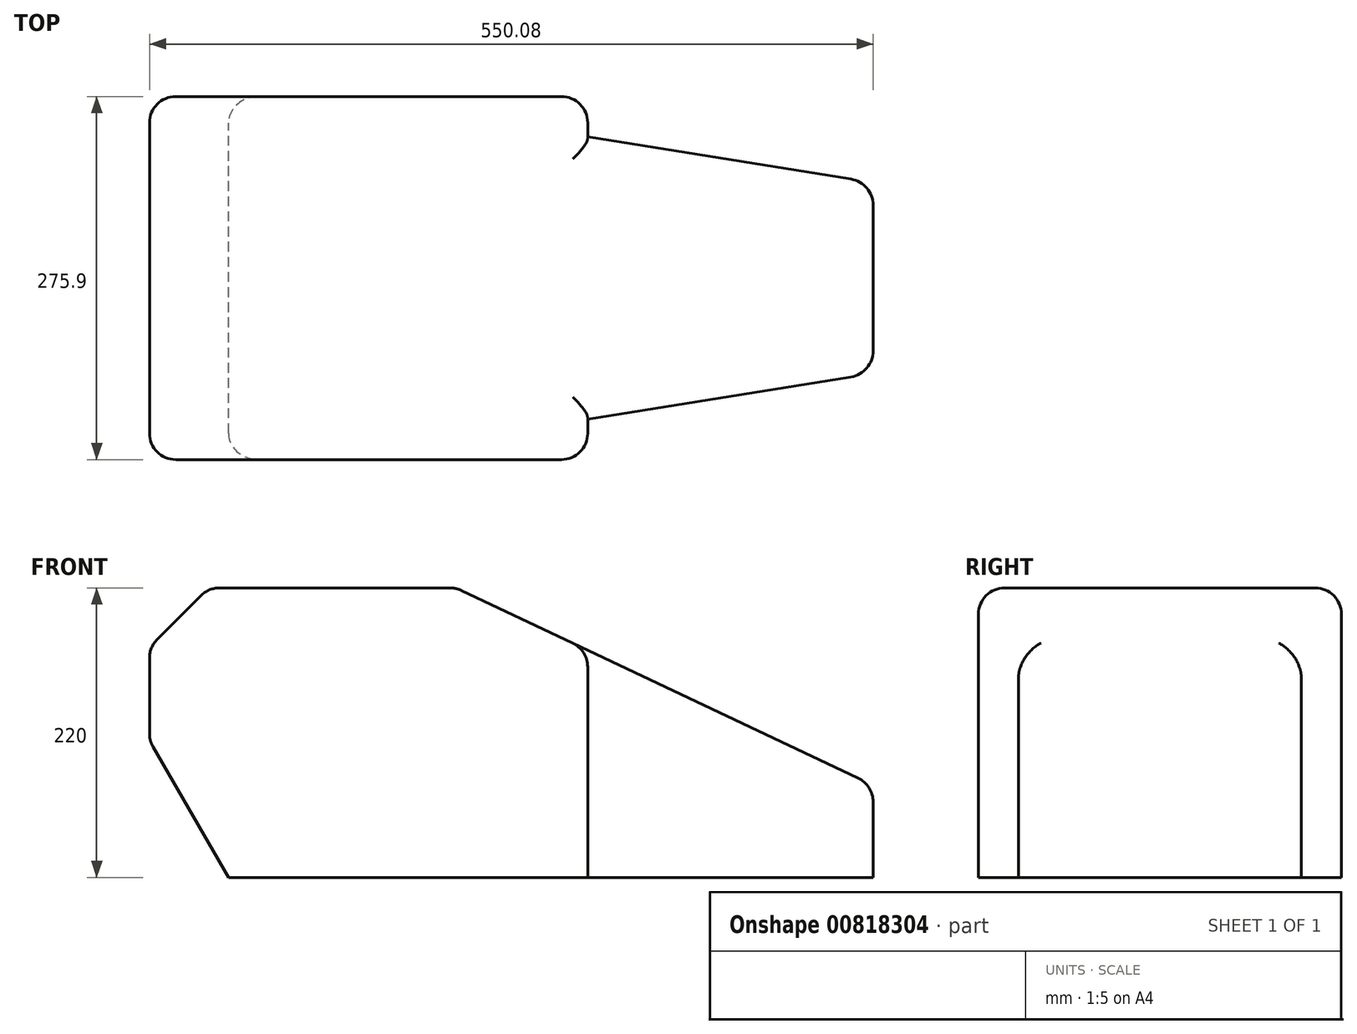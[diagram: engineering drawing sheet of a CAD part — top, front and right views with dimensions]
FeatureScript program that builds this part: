
annotation { "Feature Type Name" : "Feature", "Feature Type Description" : "" }
export const myFeature = defineFeature(function(context is Context, id is Id, definition is map)
    precondition{}
    {
        {
            var Q0;
            Q0=qCreatedBy(makeId("Top.planeOp"),FACE);
            var sketch = newSketch(context, id + "F0", { "sketchPlane" : qUnion([Q0])});
            skLineSegment(sketch, "E0.bottom", {"start": v(-166.54, 53.98) * mm, "end": v(166.54, 53.98) * mm});
            skLineSegment(sketch, "E0.top", {"start": v(-166.54, -53.98) * mm, "end": v(166.54, -53.98) * mm});
            skLineSegment(sketch, "E0.left", {"start": v(-166.54, 53.98) * mm, "end": v(-166.54, -53.98) * mm});
            skLineSegment(sketch, "E0.right", {"start": v(166.54, 53.98) * mm, "end": v(166.54, -53.98) * mm});
            skPoint(sketch, "E0.middle", {"position": v(0, 0) * mm});
            skLineSegment(sketch, "E1.top", {"start": v(-166.54, 83.98) * mm, "end": v(166.54, 83.98) * mm});
            skLineSegment(sketch, "E1.left", {"start": v(-166.54, 53.98) * mm, "end": v(-166.54, 83.98) * mm});
            skLineSegment(sketch, "E1.right", {"start": v(166.54, 53.98) * mm, "end": v(166.54, 83.98) * mm});
            skLineSegment(sketch, "E2.bottom", {"start": v(166.54, -53.98) * mm, "end": v(383.54, -53.98) * mm});
            skLineSegment(sketch, "E2.top", {"start": v(166.54, 53.45) * mm, "end": v(383.54, 53.45) * mm});
            skLineSegment(sketch, "E2.left", {"start": v(166.54, -53.98) * mm, "end": v(166.54, 53.45) * mm});
            skLineSegment(sketch, "E2.right", {"start": v(383.54, -53.98) * mm, "end": v(383.54, 53.45) * mm});
            skSolve(sketch);
        }
        {
            var Q0;
            Q0=makeQuery(id+"F0.imprint","IMPRINT",FACE,{"disambiguationData":[TD([[makeQuery(id+"F0.imprint","IMPRINT",EDGE,{"derivedFrom":sQuery(id+"F0.wireOp",EDGE,"E0.bottom")}),1.0]])]});
            var Q1;
            {var subQ0=sQuery(id+"F0.wireOp",EDGE,"E2.bottom");Q1=makeQuery(id+"F0.imprint","IMPRINT",FACE,{"disambiguationData":[TD([[makeQuery(id+"F0.imprint","IMPRINT",EDGE,{"derivedFrom":subQ0}),1.0]])]});}
            var Q2;
            {var subQ3=sQuery(id+"F0.wireOp",EDGE,"E0.bottom");Q2=makeQuery(id+"F0.imprint","IMPRINT",FACE,{"disambiguationData":[TD([[makeQuery(id+"F0.imprint","IMPRINT",EDGE,{"derivedFrom":subQ3}),-1.0]])]});}
            extrude(context, id + "F1", {"entities" : qUnion([Q0, Q1, Q2]), "depth" : 220 * mm, "offsetDistance" : 25 * mm});
        }
        {
            var Q0;
            Q0=makeQuery(id+"F1.opExtrude","CAP_EDGE",EDGE,{"disambiguationData":[OSD([sQuery(id+"F0.wireOp",EDGE,"E2.right")])],"isStart":false});
            chamfer(context, id + "F2", {"entities" : qUnion([Q0]), "chamferType" : ChamferType.TWO_OFFSETS, "width1" : 317 * mm, "oppositeDirection" : false, "width2" : 150 * mm, "tangentPropagation" : true});
        }
        {
            var Q0;
            Q0=makeQuery(id+"F1.opExtrude","CAP_EDGE",EDGE,{"disambiguationData":[OSD([sQuery(id+"F0.wireOp",EDGE,"E0.left"),sQuery(id+"F0.wireOp",EDGE,"E1.left")])],"isStart":true});
            chamfer(context, id + "F3", {"entities" : qUnion([Q0]), "chamferType" : ChamferType.OFFSET_ANGLE, "width" : 60 * mm, "oppositeDirection" : false, "angle" : 60 * degree, "tangentPropagation" : true});
        }
        {
            var Q0;
            Q0=makeQuery(id+"F1.opExtrude","CAP_EDGE",EDGE,{"disambiguationData":[OSD([sQuery(id+"F0.wireOp",EDGE,"E0.left"),sQuery(id+"F0.wireOp",EDGE,"E1.left")])],"isStart":false});
            chamfer(context, id + "F4", {"entities" : qUnion([Q0]), "width" : 45 * mm, "tangentPropagation" : true});
        }
        {
            var Q0;
            Q0=makeQuery(id+"F1.opExtrude","SWEPT_EDGE",EDGE,{"disambiguationData":[OSD([sQuery(id+"F0.wireOp",EDGE,"E2.top"),sQuery(id+"F0.wireOp",EDGE,"E2.right")])]});
            chamfer(context, id + "F5", {"entities" : qUnion([Q0]), "chamferType" : ChamferType.TWO_OFFSETS, "width1" : 217 * mm, "oppositeDirection" : false, "width2" : 35 * mm, "tangentPropagation" : true});
        }
        {
            var Q0;
            Q0=makeQuery(id+"F1.opExtrude","SWEPT_BODY",BODY,{"disambiguationData":[OSD([sQuery(id+"F0.wireOp",EDGE,"E0.top"),sQuery(id+"F0.wireOp",EDGE,"E0.left"),sQuery(id+"F0.wireOp",EDGE,"E0.right"),sQuery(id+"F0.wireOp",EDGE,"E1.top"),sQuery(id+"F0.wireOp",EDGE,"E1.left"),sQuery(id+"F0.wireOp",EDGE,"E1.right"),sQuery(id+"F0.wireOp",EDGE,"E2.bottom"),sQuery(id+"F0.wireOp",EDGE,"E2.top"),sQuery(id+"F0.wireOp",EDGE,"E2.right")])]});
            var Q1;
            Q1=makeQuery(id+"F1.opExtrude","SWEPT_FACE",FACE,{"disambiguationData":[OSD([sQuery(id+"F0.wireOp",EDGE,"E0.top"),sQuery(id+"F0.wireOp",EDGE,"E2.bottom")])]});
            mirror(context, id + "F6", {"operationType" : NewBodyOperationType.ADD, "entities" : qUnion([Q0]), "mirrorPlane" : qUnion([Q1])});
        }
        {
            var Q0;
            Q0=makeQuery(id+"F1.opExtrude","CAP_EDGE",EDGE,{"disambiguationData":[OSD([sQuery(id+"F0.wireOp",EDGE,"E1.top")])],"isStart":false});
            var Q1;
            Q1=makeQuery(id+"F2.opChamfer","BLEND_EDGE",EDGE,{"blendedFrom":[makeQuery(id+"F1.opExtrude","CAP_EDGE",EDGE,{"disambiguationData":[OSD([sQuery(id+"F0.wireOp",EDGE,"E2.right")])],"isStart":false}),makeQuery(id+"F1.opExtrude","SWEPT_FACE",FACE,{"disambiguationData":[OSD([sQuery(id+"F0.wireOp",EDGE,"E1.top")])]})],"blendedInto":[makeQuery(id+"F1.opExtrude","SWEPT_FACE",FACE,{"disambiguationData":[OSD([sQuery(id+"F0.wireOp",EDGE,"E1.top")])]})]});
            var Q2;
            Q2=makeQuery(id+"F4.opChamfer","BLEND_EDGE",EDGE,{"blendedFrom":[makeQuery(id+"F1.opExtrude","CAP_EDGE",EDGE,{"disambiguationData":[OSD([sQuery(id+"F0.wireOp",EDGE,"E0.left"),sQuery(id+"F0.wireOp",EDGE,"E1.left")])],"isStart":false}),makeQuery(id+"F1.opExtrude","SWEPT_FACE",FACE,{"disambiguationData":[OSD([sQuery(id+"F0.wireOp",EDGE,"E1.top")])]})],"blendedInto":[makeQuery(id+"F1.opExtrude","SWEPT_FACE",FACE,{"disambiguationData":[OSD([sQuery(id+"F0.wireOp",EDGE,"E1.top")])]})]});
            var Q3;
            Q3=makeQuery(id+"F1.opExtrude","SWEPT_EDGE",EDGE,{"disambiguationData":[OSD([sQuery(id+"F0.wireOp",EDGE,"E1.top"),sQuery(id+"F0.wireOp",EDGE,"E1.left")])]});
            var Q4;
            Q4=makeQuery(id+"F3.opChamfer","BLEND_EDGE",EDGE,{"blendedFrom":[makeQuery(id+"F1.opExtrude","CAP_EDGE",EDGE,{"disambiguationData":[OSD([sQuery(id+"F0.wireOp",EDGE,"E0.left"),sQuery(id+"F0.wireOp",EDGE,"E1.left")])],"isStart":true}),makeQuery(id+"F1.opExtrude","SWEPT_FACE",FACE,{"disambiguationData":[OSD([sQuery(id+"F0.wireOp",EDGE,"E1.top")])]})],"blendedInto":[makeQuery(id+"F1.opExtrude","SWEPT_FACE",FACE,{"disambiguationData":[OSD([sQuery(id+"F0.wireOp",EDGE,"E1.top")])]})]});
            var Q5;
            {var subQ0=sQuery(id+"F0.wireOp",EDGE,"E1.left");var subQ1=sQuery(id+"F0.wireOp",EDGE,"E0.left");var subQ2=makeQuery(id+"F3.opChamfer","BLEND_EDGE",EDGE,{"blendedFrom":[makeQuery(id+"F1.opExtrude","CAP_EDGE",EDGE,{"disambiguationData":[OSD([subQ1,subQ0])],"isStart":true}),makeQuery(id+"F1.opExtrude","SWEPT_FACE",FACE,{"disambiguationData":[OSD([subQ1,subQ0])]})],"blendedInto":[makeQuery(id+"F1.opExtrude","SWEPT_FACE",FACE,{"disambiguationData":[OSD([subQ1,subQ0])]})]});Q5=makeQuery(id+"F6.boolean.opBoolean","MERGE",EDGE,{"derivedFrom":[subQ2,makeQuery(id+"F6.opPattern","COPY",EDGE,{"derivedFrom":subQ2,"instanceName":"1"})]});}
            var Q6;
            {var subQ0=sQuery(id+"F0.wireOp",EDGE,"E1.left");var subQ1=sQuery(id+"F0.wireOp",EDGE,"E0.left");var subQ2=makeQuery(id+"F4.opChamfer","BLEND_EDGE",EDGE,{"blendedFrom":[makeQuery(id+"F1.opExtrude","CAP_EDGE",EDGE,{"disambiguationData":[OSD([subQ1,subQ0])],"isStart":false}),makeQuery(id+"F1.opExtrude","CAP_FACE",FACE,{"disambiguationData":[OSD([sQuery(id+"F0.wireOp",EDGE,"E0.top"),subQ1,sQuery(id+"F0.wireOp",EDGE,"E0.right"),sQuery(id+"F0.wireOp",EDGE,"E1.top"),subQ0,sQuery(id+"F0.wireOp",EDGE,"E1.right"),sQuery(id+"F0.wireOp",EDGE,"E2.bottom"),sQuery(id+"F0.wireOp",EDGE,"E2.top"),sQuery(id+"F0.wireOp",EDGE,"E2.right")])],"isStart":false})],"blendedInto":[makeQuery(id+"F1.opExtrude","CAP_FACE",FACE,{"disambiguationData":[OSD([sQuery(id+"F0.wireOp",EDGE,"E0.top"),subQ1,sQuery(id+"F0.wireOp",EDGE,"E0.right"),sQuery(id+"F0.wireOp",EDGE,"E1.top"),subQ0,sQuery(id+"F0.wireOp",EDGE,"E1.right"),sQuery(id+"F0.wireOp",EDGE,"E2.bottom"),sQuery(id+"F0.wireOp",EDGE,"E2.top"),sQuery(id+"F0.wireOp",EDGE,"E2.right")])],"isStart":false})]});Q6=makeQuery(id+"F6.boolean.opBoolean","MERGE",EDGE,{"derivedFrom":[subQ2,makeQuery(id+"F6.opPattern","COPY",EDGE,{"derivedFrom":subQ2,"instanceName":"1"})]});}
            var Q7;
            {var subQ0=sQuery(id+"F0.wireOp",EDGE,"E1.left");var subQ1=sQuery(id+"F0.wireOp",EDGE,"E0.left");var subQ2=makeQuery(id+"F4.opChamfer","BLEND_EDGE",EDGE,{"blendedFrom":[makeQuery(id+"F1.opExtrude","CAP_EDGE",EDGE,{"disambiguationData":[OSD([subQ1,subQ0])],"isStart":false}),makeQuery(id+"F1.opExtrude","SWEPT_FACE",FACE,{"disambiguationData":[OSD([subQ1,subQ0])]})],"blendedInto":[makeQuery(id+"F1.opExtrude","SWEPT_FACE",FACE,{"disambiguationData":[OSD([subQ1,subQ0])]})]});Q7=makeQuery(id+"F6.boolean.opBoolean","MERGE",EDGE,{"derivedFrom":[subQ2,makeQuery(id+"F6.opPattern","COPY",EDGE,{"derivedFrom":subQ2,"instanceName":"1"})]});}
            var Q8;
            {var subQ0=sQuery(id+"F0.wireOp",EDGE,"E2.right");var subQ1=makeQuery(id+"F2.opChamfer","BLEND_EDGE",EDGE,{"blendedFrom":[makeQuery(id+"F1.opExtrude","CAP_EDGE",EDGE,{"disambiguationData":[OSD([subQ0])],"isStart":false}),makeQuery(id+"F1.opExtrude","CAP_FACE",FACE,{"disambiguationData":[OSD([sQuery(id+"F0.wireOp",EDGE,"E0.top"),sQuery(id+"F0.wireOp",EDGE,"E0.left"),sQuery(id+"F0.wireOp",EDGE,"E0.right"),sQuery(id+"F0.wireOp",EDGE,"E1.top"),sQuery(id+"F0.wireOp",EDGE,"E1.left"),sQuery(id+"F0.wireOp",EDGE,"E1.right"),sQuery(id+"F0.wireOp",EDGE,"E2.bottom"),sQuery(id+"F0.wireOp",EDGE,"E2.top"),subQ0])],"isStart":false})],"blendedInto":[makeQuery(id+"F1.opExtrude","CAP_FACE",FACE,{"disambiguationData":[OSD([sQuery(id+"F0.wireOp",EDGE,"E0.top"),sQuery(id+"F0.wireOp",EDGE,"E0.left"),sQuery(id+"F0.wireOp",EDGE,"E0.right"),sQuery(id+"F0.wireOp",EDGE,"E1.top"),sQuery(id+"F0.wireOp",EDGE,"E1.left"),sQuery(id+"F0.wireOp",EDGE,"E1.right"),sQuery(id+"F0.wireOp",EDGE,"E2.bottom"),sQuery(id+"F0.wireOp",EDGE,"E2.top"),subQ0])],"isStart":false})]});Q8=makeQuery(id+"F6.boolean.opBoolean","MERGE",EDGE,{"derivedFrom":[subQ1,makeQuery(id+"F6.opPattern","COPY",EDGE,{"derivedFrom":subQ1,"instanceName":"1"})]});}
            var Q9;
            Q9=makeQuery(id+"F2.opChamfer","BLEND_EDGE",EDGE,{"blendedFrom":[makeQuery(id+"F1.opExtrude","CAP_EDGE",EDGE,{"disambiguationData":[OSD([sQuery(id+"F0.wireOp",EDGE,"E2.right")])],"isStart":false}),makeQuery(id+"F1.opExtrude","SWEPT_FACE",FACE,{"disambiguationData":[OSD([sQuery(id+"F0.wireOp",EDGE,"E0.right"),sQuery(id+"F0.wireOp",EDGE,"E1.right")])]})],"blendedInto":[makeQuery(id+"F1.opExtrude","SWEPT_FACE",FACE,{"disambiguationData":[OSD([sQuery(id+"F0.wireOp",EDGE,"E0.right"),sQuery(id+"F0.wireOp",EDGE,"E1.right")])]})]});
            var Q10;
            {var subQ0=sQuery(id+"F0.wireOp",EDGE,"E2.right");Q10=makeQuery(id+"F5.opChamfer","BLEND_EDGE",EDGE,{"blendedFrom":[makeQuery(id+"F1.opExtrude","SWEPT_EDGE",EDGE,{"disambiguationData":[OSD([sQuery(id+"F0.wireOp",EDGE,"E2.top"),subQ0])]}),makeQuery(id+"F2.opChamfer","BLEND_FACE",FACE,{"disambiguationData":[OSD([subQ0])]})],"blendedInto":[makeQuery(id+"F2.opChamfer","BLEND_FACE",FACE,{"disambiguationData":[OSD([subQ0])]})]});}
            var Q11;
            Q11=makeQuery(id+"F1.opExtrude","SWEPT_EDGE",EDGE,{"disambiguationData":[OSD([sQuery(id+"F0.wireOp",EDGE,"E1.top"),sQuery(id+"F0.wireOp",EDGE,"E1.right")])]});
            var Q12;
            {var subQ0=sQuery(id+"F0.wireOp",EDGE,"E2.right");Q12=makeQuery(id+"F5.opChamfer","BLEND_EDGE",EDGE,{"blendedFrom":[makeQuery(id+"F1.opExtrude","SWEPT_EDGE",EDGE,{"disambiguationData":[OSD([sQuery(id+"F0.wireOp",EDGE,"E2.top"),subQ0])]}),makeQuery(id+"F1.opExtrude","SWEPT_FACE",FACE,{"disambiguationData":[OSD([subQ0])]})],"blendedInto":[makeQuery(id+"F1.opExtrude","SWEPT_FACE",FACE,{"disambiguationData":[OSD([subQ0])]})]});}
            var Q13;
            {var subQ0=sQuery(id+"F0.wireOp",EDGE,"E2.right");var subQ1=makeQuery(id+"F2.opChamfer","BLEND_EDGE",EDGE,{"blendedFrom":[makeQuery(id+"F1.opExtrude","CAP_EDGE",EDGE,{"disambiguationData":[OSD([subQ0])],"isStart":false}),makeQuery(id+"F1.opExtrude","SWEPT_FACE",FACE,{"disambiguationData":[OSD([subQ0])]})],"blendedInto":[makeQuery(id+"F1.opExtrude","SWEPT_FACE",FACE,{"disambiguationData":[OSD([subQ0])]})]});Q13=makeQuery(id+"F6.boolean.opBoolean","MERGE",EDGE,{"derivedFrom":[subQ1,makeQuery(id+"F6.opPattern","COPY",EDGE,{"derivedFrom":subQ1,"instanceName":"1"})]});}
            var Q14;
            {var subQ0=sQuery(id+"F0.wireOp",EDGE,"E2.right");Q14=makeQuery(id+"F6.opPattern","COPY",EDGE,{"derivedFrom":makeQuery(id+"F5.opChamfer","BLEND_EDGE",EDGE,{"blendedFrom":[makeQuery(id+"F1.opExtrude","SWEPT_EDGE",EDGE,{"disambiguationData":[OSD([sQuery(id+"F0.wireOp",EDGE,"E2.top"),subQ0])]}),makeQuery(id+"F1.opExtrude","SWEPT_FACE",FACE,{"disambiguationData":[OSD([subQ0])]})],"blendedInto":[makeQuery(id+"F1.opExtrude","SWEPT_FACE",FACE,{"disambiguationData":[OSD([subQ0])]})]}),"instanceName":"1"});}
            var Q15;
            {var subQ0=sQuery(id+"F0.wireOp",EDGE,"E2.right");Q15=makeQuery(id+"F6.opPattern","COPY",EDGE,{"derivedFrom":makeQuery(id+"F5.opChamfer","BLEND_EDGE",EDGE,{"blendedFrom":[makeQuery(id+"F1.opExtrude","SWEPT_EDGE",EDGE,{"disambiguationData":[OSD([sQuery(id+"F0.wireOp",EDGE,"E2.top"),subQ0])]}),makeQuery(id+"F2.opChamfer","BLEND_FACE",FACE,{"disambiguationData":[OSD([subQ0])]})],"blendedInto":[makeQuery(id+"F2.opChamfer","BLEND_FACE",FACE,{"disambiguationData":[OSD([subQ0])]})]}),"instanceName":"1"});}
            var Q16;
            Q16=makeQuery(id+"F6.opPattern","COPY",EDGE,{"derivedFrom":makeQuery(id+"F2.opChamfer","BLEND_EDGE",EDGE,{"blendedFrom":[makeQuery(id+"F1.opExtrude","CAP_EDGE",EDGE,{"disambiguationData":[OSD([sQuery(id+"F0.wireOp",EDGE,"E2.right")])],"isStart":false}),makeQuery(id+"F1.opExtrude","SWEPT_FACE",FACE,{"disambiguationData":[OSD([sQuery(id+"F0.wireOp",EDGE,"E0.right"),sQuery(id+"F0.wireOp",EDGE,"E1.right")])]})],"blendedInto":[makeQuery(id+"F1.opExtrude","SWEPT_FACE",FACE,{"disambiguationData":[OSD([sQuery(id+"F0.wireOp",EDGE,"E0.right"),sQuery(id+"F0.wireOp",EDGE,"E1.right")])]})]}),"instanceName":"1"});
            var Q17;
            Q17=makeQuery(id+"F6.opPattern","COPY",EDGE,{"derivedFrom":makeQuery(id+"F1.opExtrude","SWEPT_EDGE",EDGE,{"disambiguationData":[OSD([sQuery(id+"F0.wireOp",EDGE,"E1.top"),sQuery(id+"F0.wireOp",EDGE,"E1.right")])]}),"instanceName":"1"});
            var Q18;
            Q18=makeQuery(id+"F6.opPattern","COPY",EDGE,{"derivedFrom":makeQuery(id+"F2.opChamfer","BLEND_EDGE",EDGE,{"blendedFrom":[makeQuery(id+"F1.opExtrude","CAP_EDGE",EDGE,{"disambiguationData":[OSD([sQuery(id+"F0.wireOp",EDGE,"E2.right")])],"isStart":false}),makeQuery(id+"F1.opExtrude","SWEPT_FACE",FACE,{"disambiguationData":[OSD([sQuery(id+"F0.wireOp",EDGE,"E1.top")])]})],"blendedInto":[makeQuery(id+"F1.opExtrude","SWEPT_FACE",FACE,{"disambiguationData":[OSD([sQuery(id+"F0.wireOp",EDGE,"E1.top")])]})]}),"instanceName":"1"});
            var Q19;
            Q19=makeQuery(id+"F6.opPattern","COPY",EDGE,{"derivedFrom":makeQuery(id+"F1.opExtrude","CAP_EDGE",EDGE,{"disambiguationData":[OSD([sQuery(id+"F0.wireOp",EDGE,"E1.top")])],"isStart":false}),"instanceName":"1"});
            var Q20;
            Q20=makeQuery(id+"F6.opPattern","COPY",EDGE,{"derivedFrom":makeQuery(id+"F4.opChamfer","BLEND_EDGE",EDGE,{"blendedFrom":[makeQuery(id+"F1.opExtrude","CAP_EDGE",EDGE,{"disambiguationData":[OSD([sQuery(id+"F0.wireOp",EDGE,"E0.left"),sQuery(id+"F0.wireOp",EDGE,"E1.left")])],"isStart":false}),makeQuery(id+"F1.opExtrude","SWEPT_FACE",FACE,{"disambiguationData":[OSD([sQuery(id+"F0.wireOp",EDGE,"E1.top")])]})],"blendedInto":[makeQuery(id+"F1.opExtrude","SWEPT_FACE",FACE,{"disambiguationData":[OSD([sQuery(id+"F0.wireOp",EDGE,"E1.top")])]})]}),"instanceName":"1"});
            var Q21;
            Q21=makeQuery(id+"F6.opPattern","COPY",EDGE,{"derivedFrom":makeQuery(id+"F1.opExtrude","SWEPT_EDGE",EDGE,{"disambiguationData":[OSD([sQuery(id+"F0.wireOp",EDGE,"E1.top"),sQuery(id+"F0.wireOp",EDGE,"E1.left")])]}),"instanceName":"1"});
            var Q22;
            Q22=makeQuery(id+"F6.opPattern","COPY",EDGE,{"derivedFrom":makeQuery(id+"F3.opChamfer","BLEND_EDGE",EDGE,{"blendedFrom":[makeQuery(id+"F1.opExtrude","CAP_EDGE",EDGE,{"disambiguationData":[OSD([sQuery(id+"F0.wireOp",EDGE,"E0.left"),sQuery(id+"F0.wireOp",EDGE,"E1.left")])],"isStart":true}),makeQuery(id+"F1.opExtrude","SWEPT_FACE",FACE,{"disambiguationData":[OSD([sQuery(id+"F0.wireOp",EDGE,"E1.top")])]})],"blendedInto":[makeQuery(id+"F1.opExtrude","SWEPT_FACE",FACE,{"disambiguationData":[OSD([sQuery(id+"F0.wireOp",EDGE,"E1.top")])]})]}),"instanceName":"1"});
            fillet(context, id + "F7", {"entities" : qUnion([Q0, Q1, Q2, Q3, Q4, Q5, Q6, Q7, Q8, Q9, Q10, Q11, Q12, Q13, Q14, Q15, Q16, Q17, Q18, Q19, Q20, Q21, Q22]), "radius" : 20 * mm, "tangentPropagation" : true, "allowEdgeOverflow" : false});
        }
    });
